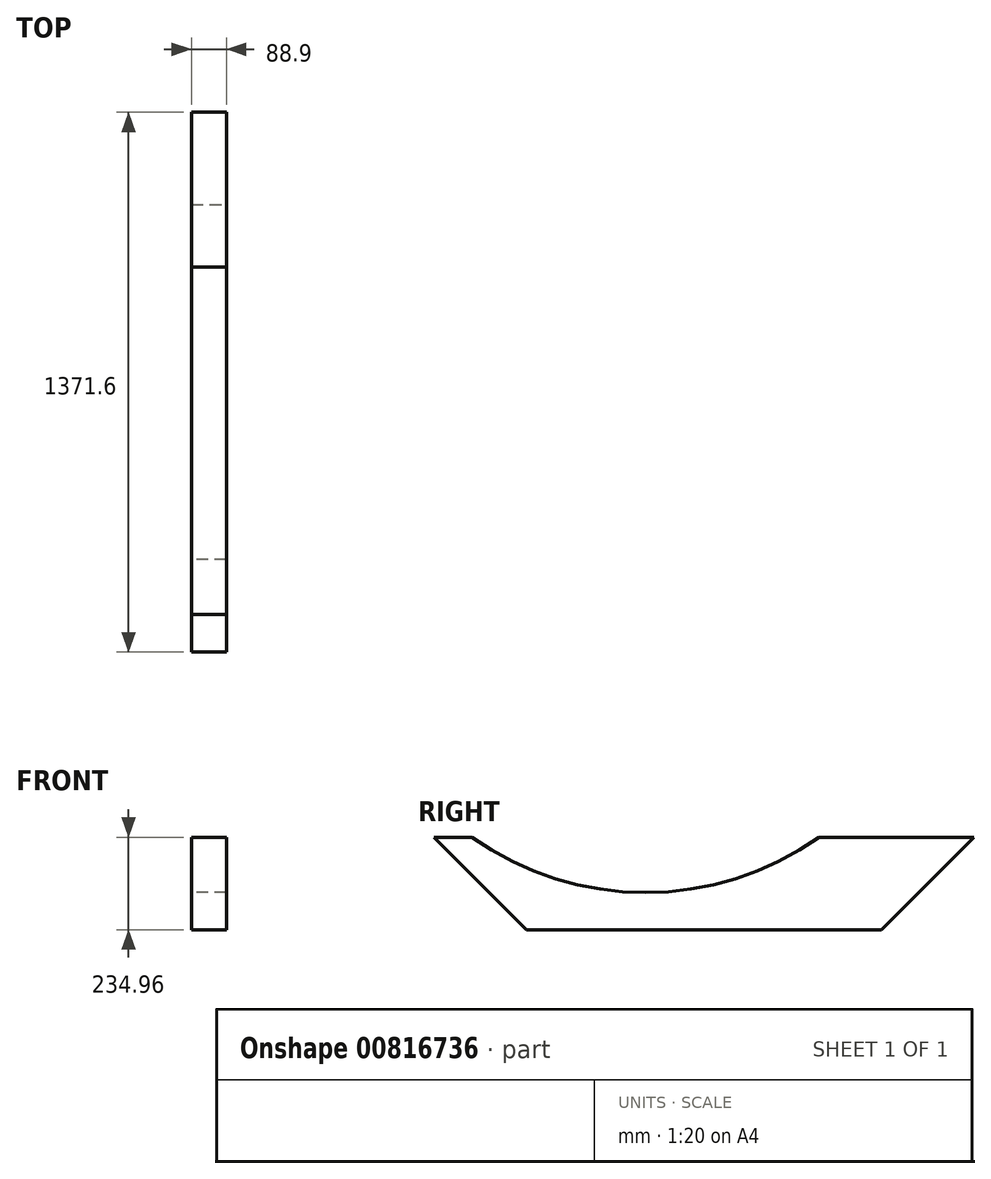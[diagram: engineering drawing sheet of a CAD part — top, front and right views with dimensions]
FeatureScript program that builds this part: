
annotation { "Feature Type Name" : "Feature", "Feature Type Description" : "" }
export const myFeature = defineFeature(function(context is Context, id is Id, definition is map)
    precondition{}
    {
        {
            var Q0;
            Q0=qCreatedBy(makeId("Front.planeOp"),FACE);
            var sketch = newSketch(context, id + "F0", { "sketchPlane" : qUnion([Q0])});
            skLineSegment(sketch, "E0.bottom", {"start": v(44.45, -117.48) * mm, "end": v(-44.45, -117.48) * mm});
            skLineSegment(sketch, "E0.top", {"start": v(44.45, 117.47) * mm, "end": v(-44.45, 117.47) * mm});
            skLineSegment(sketch, "E0.left", {"start": v(44.45, -117.48) * mm, "end": v(44.45, 117.47) * mm});
            skLineSegment(sketch, "E0.right", {"start": v(-44.45, -117.48) * mm, "end": v(-44.45, 117.47) * mm});
            skPoint(sketch, "E0.middle", {"position": v(0, 0) * mm});
            skSolve(sketch);
        }
        {
            var Q0;
            Q0 = qSketchRegion(id + "F0", true);
            extrude(context, id + "F1", {"entities" : qUnion([Q0]), "endBound" : BoundingType.SYMMETRIC, "depth" : 1371.6 * mm, "offsetDistance" : 25.4 * mm});
        }
        {
            var Q0;
            Q0=makeQuery(id+"F1.opExtrude","CAP_EDGE",EDGE,{"disambiguationData":[OSD([sQuery(id+"F0.wireOp",EDGE,"E0.bottom")])],"isStart":false});
            chamfer(context, id + "F2", {"entities" : qUnion([Q0]), "width" : 234.95 * mm, "tangentPropagation" : true});
        }
        {
            var Q0;
            Q0=makeQuery(id+"F1.opExtrude","CAP_EDGE",EDGE,{"disambiguationData":[OSD([sQuery(id+"F0.wireOp",EDGE,"E0.bottom")])],"isStart":true});
            chamfer(context, id + "F3", {"entities" : qUnion([Q0]), "width" : 234.95 * mm, "tangentPropagation" : true});
        }
        {
            var Q0;
            Q0=makeQuery(id+"F1.opExtrude","SWEPT_FACE",FACE,{"disambiguationData":[OSD([sQuery(id+"F0.wireOp",EDGE,"E0.right")])]});
            var sketch = newSketch(context, id + "F4", { "sketchPlane" : qUnion([Q0])});
            skPoint(sketch, "E1", {"position": v(148.82, 738.77) * mm});
            skSolve(sketch);
        }
        {
            var Q0;
            Q0=sQuery(id+"F4.wireOp",VERTEX,"E1");
            var Q1;
            Q1=makeQuery(id+"F1.opExtrude","SWEPT_BODY",BODY,{"disambiguationData":[OSD([sQuery(id+"F0.wireOp",EDGE,"E0.bottom"),sQuery(id+"F0.wireOp",EDGE,"E0.top"),sQuery(id+"F0.wireOp",EDGE,"E0.left"),sQuery(id+"F0.wireOp",EDGE,"E0.right")])]});
            hole(context, id + "F5", {"style" : HoleStyle.SIMPLE, "endStyle" : HoleEndStyle.THROUGH, "holeDiameter" : 1524 * mm, "majorDiameter" : 6.35 * mm, "isTappedThrough" : true, "tappedDepth" : 12.7 * mm, "tapClearance" : 3, "locations" : qUnion([Q0]), "scope" : qUnion([Q1])});
        }
    });
